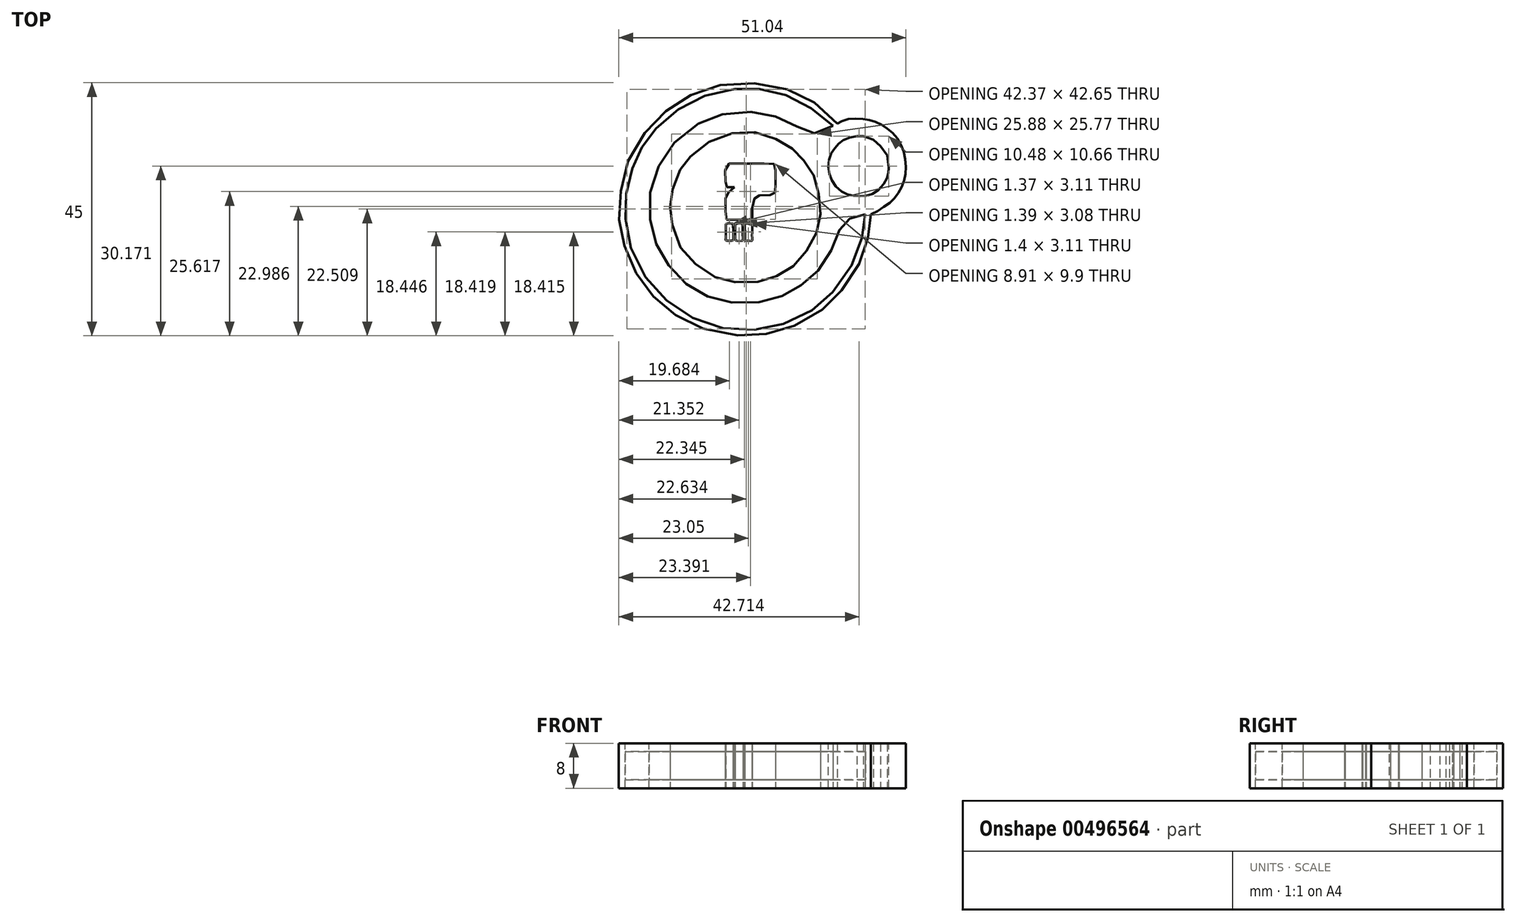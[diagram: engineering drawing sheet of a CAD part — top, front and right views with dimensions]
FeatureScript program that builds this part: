
annotation { "Feature Type Name" : "Feature", "Feature Type Description" : "" }
export const myFeature = defineFeature(function(context is Context, id is Id, definition is map)
    precondition{}
    {
        {
            var Q0;
            Q0=qCreatedBy(makeId("Top.planeOp"),FACE);
            var sketch = newSketch(context, id + "F0", { "sketchPlane" : qUnion([Q0])});
            skFitSpline(sketch, "E0", {"points": [v(49.63, 25.36) * mm, v(49.46, 23.01) * mm, v(48.79, 19.99) * mm, v(47.44, 16.38) * mm, v(44.76, 12.35) * mm, v(42.5, 9.75) * mm, v(39.3, 7.23) * mm, v(34.69, 5.05) * mm, v(31, 4.13) * mm, v(27.47, 3.8) * mm, v(21.76, 4.46) * mm, v(16.98, 6.3) * mm, v(13.7, 8.32) * mm, v(10.68, 11) * mm, v(8.42, 14.03) * mm, v(6.32, 18.14) * mm, v(5.4, 21.33) * mm, v(4.8, 24.86) * mm, v(5.06, 28.72) * mm, v(5.65, 32.58) * mm, v(7.83, 37.7) * mm, v(10.6, 41.22) * mm, v(13.79, 44.24) * mm, v(17.23, 46.43) * mm, v(21.5, 48.02) * mm, v(26.2, 48.78) * mm, v(32.59, 48.19) * mm, v(36.36, 46.93) * mm, v(40.3, 44.75) * mm, v(43.67, 41.47) * mm], "startDerivative": vector(-2.43, -96.79) * mm, "endDerivative": vector(87.16, -96.5) * mm});
            skFitSpline(sketch, "E1", {"points": [v(43.67, 41.47) * mm, v(44.92, 42.15) * mm, v(47.28, 42.4) * mm, v(49.37, 42.15) * mm, v(51.14, 41.47) * mm, v(52.98, 40.3) * mm, v(54.5, 38.62) * mm, v(55.5, 36.36) * mm, v(55.84, 33.75) * mm, v(55.58, 31.49) * mm, v(54.74, 29.56) * mm, v(53.57, 27.96) * mm, v(51.8, 26.62) * mm, v(49.63, 25.36) * mm], "startDerivative": vector(17.96, 12.23) * mm, "endDerivative": vector(-27.9, -10.17) * mm});
            skLineSegment(sketch, "E2", {"start": v(47.1, 39.3) * mm, "end": v(48.28, 39.3) * mm});
            skLineSegment(sketch, "E3", {"start": v(48.28, 39.3) * mm, "end": v(50.04, 38.62) * mm});
            skLineSegment(sketch, "E4", {"start": v(50.04, 38.62) * mm, "end": v(51.3, 37.53) * mm});
            skLineSegment(sketch, "E5", {"start": v(51.3, 37.53) * mm, "end": v(52.56, 35.85) * mm});
            skFitSpline(sketch, "E6", {"points": [v(47.1, 39.3) * mm, v(44.84, 38.62) * mm, v(43.5, 37.53) * mm, v(42.5, 36.02) * mm, v(42.07, 33.67) * mm, v(42.66, 31.4) * mm, v(44.34, 29.47) * mm, v(46.27, 28.72) * mm, v(48.2, 28.63) * mm, v(50.04, 29.05) * mm, v(52.06, 30.98) * mm, v(52.73, 32.66) * mm, v(52.73, 34) * mm, v(52.56, 35.85) * mm], "startDerivative": vector(-29.6, -6.3) * mm, "endDerivative": vector(-2.5, 26.37) * mm});
            skFitSpline(sketch, "E7", {"points": [v(42.91, 41.14) * mm, v(40.48, 43.24) * mm, v(37.04, 45.34) * mm, v(34.01, 46.76) * mm, v(30.4, 47.6) * mm, v(28.81, 47.69) * mm, v(25.54, 47.69) * mm, v(21.6, 46.93) * mm, v(17.4, 45.34) * mm, v(14.54, 43.4) * mm, v(11.6, 40.89) * mm, v(9.76, 38.62) * mm, v(8.67, 36.86) * mm, v(7.58, 34.6) * mm, v(6.82, 32.41) * mm, v(6.15, 29.22) * mm, v(5.9, 25.36) * mm, v(5.98, 24.52) * mm, v(6.57, 20.74) * mm, v(8.42, 16.13) * mm, v(10.93, 12.35) * mm, v(14.12, 9.41) * mm, v(17.73, 7.06) * mm, v(22.18, 5.39) * mm, v(26.2, 4.8) * mm, v(30.9, 5.05) * mm, v(34.27, 5.97) * mm, v(38.38, 7.82) * mm, v(41.4, 10.17) * mm, v(43.58, 12.35) * mm, v(46.44, 16.72) * mm, v(47.78, 20.16) * mm, v(48.53, 23.6) * mm, v(48.62, 25.36) * mm], "startDerivative": vector(-77.4, 73.3) * mm, "endDerivative": vector(-4.92, 83.75) * mm});
            skFitSpline(sketch, "E8", {"points": [v(48.62, 25.36) * mm, v(47.28, 25.36) * mm, v(45.68, 24.52) * mm, v(44.67, 23.77) * mm, v(43.83, 22.17) * mm, v(42.83, 19.57) * mm, v(41.32, 16.8) * mm, v(38.88, 14.03) * mm, v(36.78, 12.52) * mm, v(34.52, 11.18) * mm, v(31.5, 10.09) * mm, v(27.97, 9.58) * mm, v(23.52, 9.92) * mm, v(20.25, 10.92) * mm, v(17.14, 12.69) * mm, v(14.46, 15.29) * mm, v(12.36, 18.31) * mm, v(10.93, 21.58) * mm, v(10.26, 25.36) * mm, v(10.43, 29.64) * mm, v(11.86, 33.84) * mm, v(14.37, 37.78) * mm, v(18.57, 41.3) * mm, v(21.93, 42.82) * mm, v(26.63, 43.66) * mm, v(30.66, 43.24) * mm, v(34.01, 42.31) * mm, v(36.7, 40.8) * mm, v(38.46, 39.96) * mm, v(40.73, 39.96) * mm, v(42.91, 41.14) * mm], "startDerivative": vector(-60.95, 8.65) * mm, "endDerivative": vector(71.48, 48.96) * mm});
            skFitSpline(sketch, "E9", {"points": [v(15.72, 33.33) * mm, v(17.06, 35.18) * mm, v(20.5, 38.03) * mm, v(25.45, 39.88) * mm, v(29.82, 39.8) * mm, v(33.76, 38.29) * mm, v(36.11, 36.7) * mm, v(37.62, 35.01) * mm, v(39.3, 32.66) * mm, v(40.22, 29.64) * mm, v(40.64, 26.03) * mm, v(40.22, 22.93) * mm, v(38.63, 19.65) * mm, v(36.45, 16.72) * mm, v(33.51, 14.7) * mm, v(30.82, 13.61) * mm, v(26.2, 13.27) * mm, v(22.52, 13.95) * mm, v(18.49, 16.46) * mm, v(15.63, 19.74) * mm, v(14.12, 24.44) * mm, v(13.95, 26.87) * mm, v(14.3, 29.64) * mm, v(15.72, 33.33) * mm]});
            skFitSpline(sketch, "E10", {"points": [v(25.36, 30.2) * mm, v(24.6, 30.27) * mm, v(23.83, 30.27) * mm, v(23.77, 30.8) * mm, v(23.76, 32.53) * mm, v(23.9, 34.17) * mm, v(25.18, 34.4) * mm, v(27.4, 34.36) * mm, v(29.44, 34.36) * mm, v(31.7, 34.37) * mm, v(32.53, 34.28) * mm, v(32.65, 33.74) * mm, v(32.63, 31.25) * mm, v(32.64, 29.74) * mm, v(32.5, 28.91) * mm, v(31.9, 28.8) * mm, v(29.98, 28.78) * mm, v(29.48, 28.63) * mm, v(28.98, 28.21) * mm, v(28.64, 27.54) * mm, v(28.53, 24.9) * mm, v(28.45, 24.46) * mm, v(27.64, 24.44) * mm, v(26.38, 24.44) * mm, v(24.37, 24.35) * mm, v(23.88, 24.5) * mm, v(23.77, 25.61) * mm, v(23.76, 28.17) * mm, v(23.9, 28.86) * mm, v(24.7, 29.59) * mm, v(25.36, 30.2) * mm]});
            skFitSpline(sketch, "E11", {"points": [v(25.09, 23.7) * mm, v(23.88, 23.68) * mm, v(23.8, 23.42) * mm, v(23.84, 22.17) * mm, v(23.8, 21.02) * mm, v(23.88, 20.73) * mm, v(25.11, 20.73) * mm], "startDerivative": vector(-4.55, 1.08) * mm, "endDerivative": vector(4.27, 1.31) * mm});
            skFitSpline(sketch, "E12", {"points": [v(25.11, 20.73) * mm, v(25.09, 23.7) * mm], "startDerivative": vector(0.3, 3) * mm, "endDerivative": vector(-0.22, 3.02) * mm});
            skFitSpline(sketch, "E13", {"points": [v(25.64, 23.7) * mm, v(26.52, 23.76) * mm, v(26.75, 23.7) * mm, v(26.83, 23.06) * mm, v(26.85, 20.94) * mm, v(26.83, 20.71) * mm, v(26.52, 20.65) * mm, v(25.55, 20.73) * mm, v(25.5, 21.04) * mm, v(25.46, 22.89) * mm, v(25.51, 23.6) * mm, v(25.64, 23.7) * mm]});
            skFitSpline(sketch, "E14", {"points": [v(27.23, 23.76) * mm, v(27.2, 23.45) * mm, v(27.16, 22.41) * mm, v(27.15, 21.1) * mm, v(27.23, 20.71) * mm, v(27.78, 20.69) * mm, v(28.48, 20.66) * mm, v(28.5, 21.3) * mm, v(28.53, 22.49) * mm, v(28.55, 23.36) * mm, v(28.47, 23.72) * mm, v(27.9, 23.8) * mm, v(27.23, 23.76) * mm]});
            skSolve(sketch);
        }
        {
            var Q0;
            Q0=makeQuery(id+"F0.imprint","IMPRINT",FACE,{"disambiguationData":[TD([[makeQuery(id+"F0.imprint","IMPRINT",EDGE,{"derivedFrom":sQuery(id+"F0.wireOp",EDGE,"E0")}),-1.0]])]});
            var Q1;
            Q1=makeQuery(id+"F0.imprint","IMPRINT",FACE,{"disambiguationData":[TD([[makeQuery(id+"F0.imprint","IMPRINT",EDGE,{"derivedFrom":sQuery(id+"F0.wireOp",EDGE,"E10")}),-1.0]])]});
            var Q2;
            Q2=makeQuery(id+"F0.imprint","IMPRINT",FACE,{"disambiguationData":[TD([[makeQuery(id+"F0.imprint","IMPRINT",EDGE,{"derivedFrom":sQuery(id+"F0.wireOp",EDGE,"E13")}),-1.0]])]});
            var Q3;
            Q3=makeQuery(id+"F0.imprint","IMPRINT",FACE,{"disambiguationData":[TD([[makeQuery(id+"F0.imprint","IMPRINT",EDGE,{"derivedFrom":sQuery(id+"F0.wireOp",EDGE,"E11")}),1.0]])]});
            var Q4;
            Q4=makeQuery(id+"F0.imprint","IMPRINT",FACE,{"disambiguationData":[TD([[makeQuery(id+"F0.imprint","IMPRINT",EDGE,{"derivedFrom":sQuery(id+"F0.wireOp",EDGE,"E14")}),1.0]])]});
            extrude(context, id + "F1", {"entities" : qUnion([Q0, Q1, Q2, Q3, Q4]), "endBound" : BoundingType.SYMMETRIC, "depth" : 8 * mm, "offsetDistance" : 25 * mm});
        }
        {
            var Q0;
            Q0=makeQuery(id+"F0.imprint","IMPRINT",FACE,{"disambiguationData":[TD([[makeQuery(id+"F0.imprint","IMPRINT",EDGE,{"derivedFrom":sQuery(id+"F0.wireOp",EDGE,"E7")}),1.0]])]});
            var Q1;
            Q1=makeQuery(id+"F0.imprint","IMPRINT",FACE,{"disambiguationData":[TD([[makeQuery(id+"F0.imprint","IMPRINT",EDGE,{"derivedFrom":sQuery(id+"F0.wireOp",EDGE,"E9")}),-1.0]])]});
            extrude(context, id + "F2", {"entities" : qUnion([Q0, Q1]), "endBound" : BoundingType.SYMMETRIC, "depth" : 5 * mm, "offsetDistance" : 25 * mm});
        }
    });
